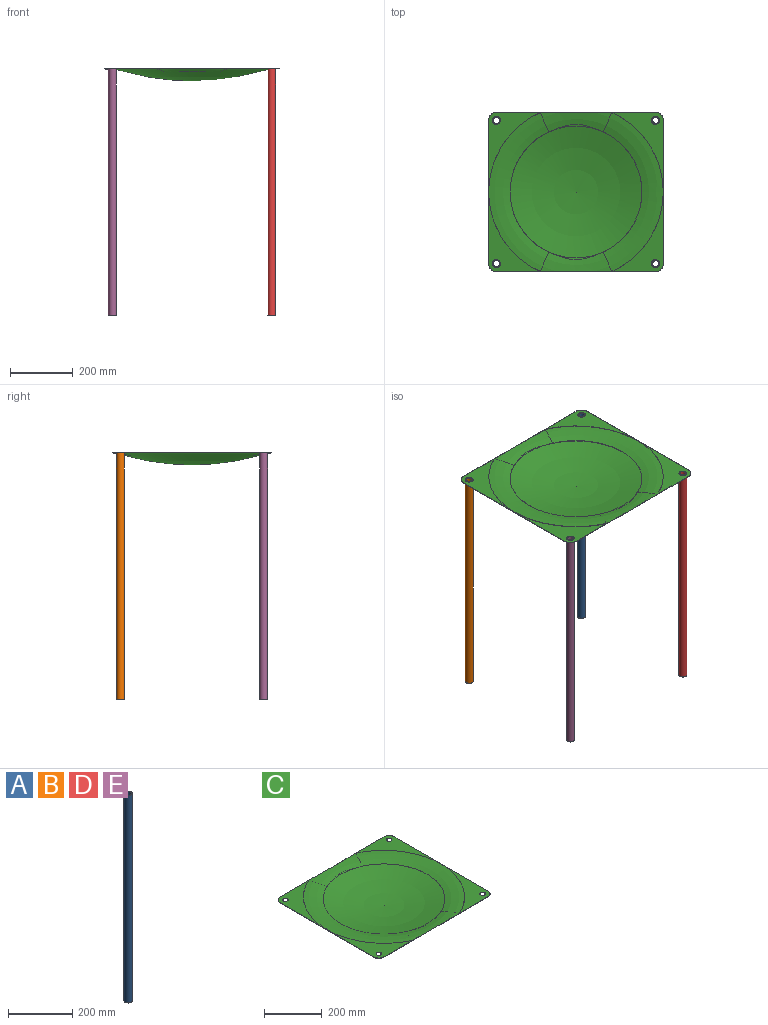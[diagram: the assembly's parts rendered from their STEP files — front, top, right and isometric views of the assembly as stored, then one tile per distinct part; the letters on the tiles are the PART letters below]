
ASSEMBLY  parts=5 mates=1
PART A: 4 faces, bbox 25.4x25.4x787.4 mm
  f0: cylinder r=11.11mm len=787.4mm, axis (0,0,-1), area 54977.8mm2, adj f2,f3
  f1: cylinder r=12.7mm len=787.4mm, axis (0,0,-1), area 62831.7mm2, adj f2,f3
  f2: plane 25.4x25.4mm, normal (0,0,1), area 118.8mm2, adj f0,f1
  f3: plane 25.4x25.4mm, normal (0,0,-1), area 118.8mm2, adj f0,f1
PART B: same geometry as A
PART C: 23 faces, bbox 603.4x603x75.2 mm
  f0: plane 508x165.1mm, normal (0,0,1), area 22998.1mm2, adj f3,f4,f5,f14,f15,f16,f21,f22
  f1: plane 508x164.57mm, normal (0,0,-1), area 22859.4mm2, adj f3,f4,f5,f12,f15,f16,f21,f22
  f2: sphere r=783.17mm, area 141567.9mm2, adj f14
  f3: plane 508x1.59mm, normal (0,1,0), area 663.7mm2, adj f0,f1,f7,f8,f13,f14,f15,f18
  f4: plane 457.2x1.59mm, normal (-1,0,0), area 725.8mm2, adj f0,f1,f15,f16
  f5: plane 508x1.59mm, normal (0,-1,0), area 663.7mm2, adj f0,f1,f7,f8,f10,f14,f16,f17
  f6: plane 457.2x1.59mm, normal (1,0,0), area 725.8mm2, adj f7,f8,f17,f18
  f7: plane 508x164.57mm, normal (0,0,-1), area 22859.4mm2, adj f3,f5,f6,f11,f17,f18,f19,f20
  f8: plane 508x165.1mm, normal (0,0,1), area 22998.1mm2, adj f3,f5,f6,f14,f17,f18,f19,f20
  f9: sphere r=784.75mm, area 142899.6mm2, adj f10,f11,f12,f13
  f10: bspline ~249.25x66.34mm, area 10033mm2, adj f5,f9,f11,f12
  f11: torus R=278.75mm, axis (0,0,1), area 38671.6mm2, adj f7,f9,f10,f13
  f12: torus R=278.75mm, axis (0,0,1), area 38671.6mm2, adj f1,f9,f10,f13
  f13: bspline ~249.25x66.34mm, area 10033mm2, adj f3,f9,f11,f12
  f14: torus R=278.53mm, axis (0,0,1), area 98414.7mm2, adj f0,f2,f3,f5,f8
  f15: cylinder r=25.4mm len=25.4mm, axis (0,0,-1), area 63.3mm2, adj f0,f1,f3,f4
  f16: cylinder r=25.4mm len=25.4mm, axis (0,0,1), area 63.3mm2, adj f0,f1,f4,f5
  f17: cylinder r=25.4mm len=25.4mm, axis (0,0,-1), area 63.3mm2, adj f5,f6,f7,f8
  f18: cylinder r=25.4mm len=25.4mm, axis (0,0,1), area 63.3mm2, adj f3,f6,f7,f8
  f19: cylinder r=9.53mm len=19.05mm, axis (0,0,1), area 95mm2, adj f7,f8
  f20: cylinder r=9.53mm len=19.05mm, axis (0,0,1), area 95mm2, adj f7,f8
  f21: cylinder r=9.53mm len=19.05mm, axis (0,0,1), area 95mm2, adj f0,f1
  f22: cylinder r=9.53mm len=19.05mm, axis (0,0,1), area 95mm2, adj f0,f1
PART D: same geometry as A
PART E: same geometry as A
PLACE A t=(508,457.2,0)mm
PLACE B t=(0,457.2,0)mm
PLACE C t=(254,228.6,788.99)mm
PLACE D t=(508,0,0)mm
PLACE E at identity fixed
MATE planar C.f1 <-> E.f1  axis (0,0,-1) through (69.59,-25.4,787.4)mm
